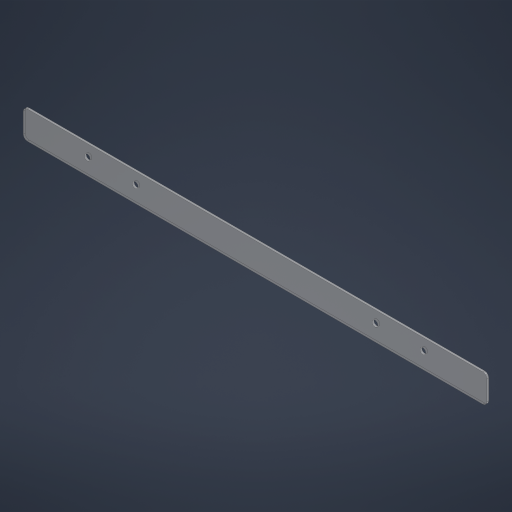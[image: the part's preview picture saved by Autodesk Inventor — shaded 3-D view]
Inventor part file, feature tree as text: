
AUTODESK INVENTOR PART (.ipt)
format: ipt  version: 2024 (Build 280153000, 153)  size: 234,496 bytes
history: native  units: in
note: dims shown in document units (in); Inventor stores cm internally (conversion verified against a paired STEP export)
features: sketch x2, extrude x1, hole x1
ambient origin geometry x8: Origin, YZ Plane, XZ Plane, XY Plane, X Axis, Y Axis, Z Axis, Center Point
bodies: Solid1 (feature_tree)
feature tree (4):
  extrude  "Extrusion1"  Depth=0.0625in
  hole  "Hole1"  [1 undecoded]
  sketch  "Sketch1"  dims[d2=0.0625in d3=0.0in d4=2.25in]
  sketch  "Sketch2"  dims[d5=2.0in d12=0.1875in d13=0.75in d14=0.375in d15=0.25in d16=0.5635in d17=1.0in d18=0.8108in d21=0.5in d22=0.5in d24=0.375in d25=0.375in d26=0.125in d27=0.875in d28=0.125in d29=14.25in]
note: 1 required parameter value undecoded (feature->parameter linkage not recoverable at this tier; creation-order binding heuristic only, values carry confidence <= 0.55)
